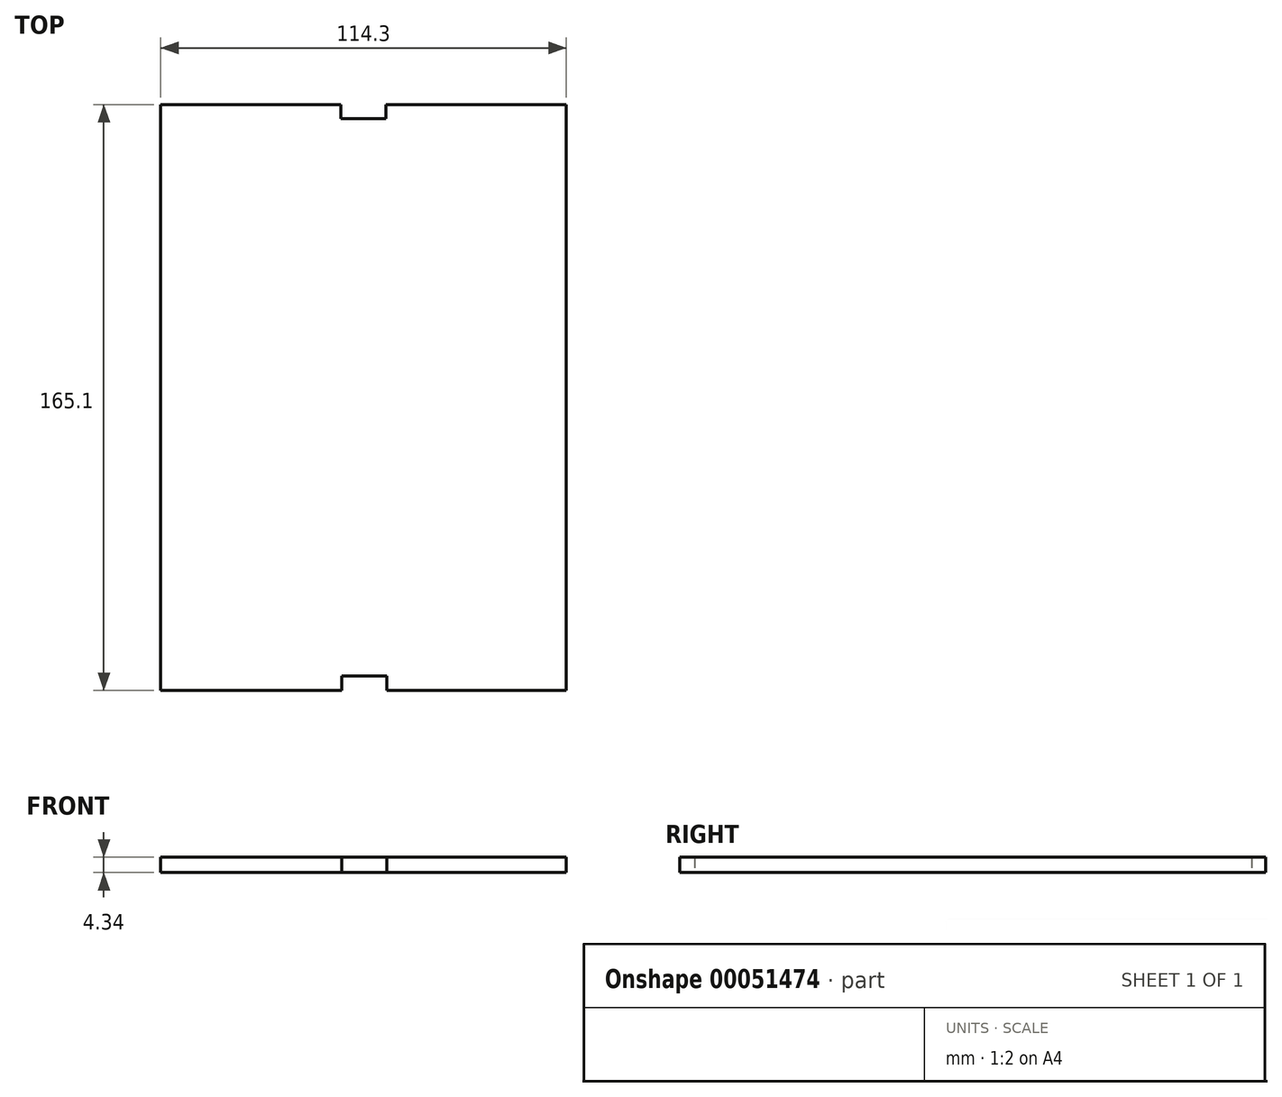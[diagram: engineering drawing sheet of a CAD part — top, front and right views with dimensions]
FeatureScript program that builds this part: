
annotation { "Feature Type Name" : "Feature", "Feature Type Description" : "" }
export const myFeature = defineFeature(function(context is Context, id is Id, definition is map)
    precondition{}
    {
        {
            var Q0;
            Q0=qCreatedBy(makeId("Top.planeOp"),FACE);
            var sketch = newSketch(context, id + "F0", { "sketchPlane" : qUnion([Q0])});
            skLineSegment(sketch, "E0.bottom", {"start": v(-56.26, 135.4) * mm, "end": v(58.04, 135.4) * mm});
            skLineSegment(sketch, "E0.top", {"start": v(-56.26, -29.7) * mm, "end": v(58.04, -29.7) * mm});
            skLineSegment(sketch, "E0.left", {"start": v(-56.26, 135.4) * mm, "end": v(-56.26, -29.7) * mm});
            skLineSegment(sketch, "E0.right", {"start": v(58.04, 135.4) * mm, "end": v(58.04, -29.7) * mm});
            skSolve(sketch);
        }
        {
            var Q0;
            Q0 = qSketchRegion(id + "F0", true);
            extrude(context, id + "F1", {"entities" : qUnion([Q0]), "depth" : 4.34 * mm});
        }
        {
            var Q0;
            Q0=qCreatedBy(makeId("Top.planeOp"),FACE);
            var sketch = newSketch(context, id + "F2", { "sketchPlane" : qUnion([Q0])});
            skLineSegment(sketch, "E1.0", {"start": v(-5.46, 135.4) * mm, "end": v(-5.46, -29.37) * mm, "construction": true});
            skLineSegment(sketch, "E2", {"start": v(-57.24, 53.01) * mm, "end": v(58.42, 53.01) * mm, "construction": true});
            skPoint(sketch, "E2.startSnap0", {"position": v(-5.46, 53.01) * mm});
            skPoint(sketch, "E3.orphan", {"position": v(7.24, 131.05) * mm});
            skPoint(sketch, "E4.MirrorCS.start.orphan", {"position": v(-5.46, 131.05) * mm});
            skPoint(sketch, "E5.orphan", {"position": v(-5.46, 135.4) * mm});
            skPoint(sketch, "E6.MirrorCS.end.orphan", {"position": v(7.24, 135.4) * mm});
            skPoint(sketch, "E7.end.orphan", {"position": v(7.24, -25.02) * mm});
            skPoint(sketch, "E8.left.end.orphan", {"position": v(-5.46, -25.02) * mm});
            skLineSegment(sketch, "E9.left", {"start": v(-5.46, 131.05) * mm, "end": v(-5.46, 135.4) * mm});
            skLineSegment(sketch, "E9.right", {"start": v(7.24, 131.05) * mm, "end": v(7.24, 135.4) * mm});
            skPoint(sketch, "E10.orphan", {"position": v(7.24, -29.37) * mm});
            skPoint(sketch, "E11.start.orphan", {"position": v(0.89, 135.4) * mm});
            skPoint(sketch, "E12.trimOffspring.end.orphan", {"position": v(0.89, -29.37) * mm});
            skSolve(sketch);
        }
        {
            var Q0;
            Q0=qCreatedBy(makeId("Top.planeOp"),FACE);
            var sketch = newSketch(context, id + "F3", { "sketchPlane" : qUnion([Q0])});
            skLineSegment(sketch, "E13.top", {"start": v(-5.18, 131.6) * mm, "end": v(7.52, 131.6) * mm});
            skLineSegment(sketch, "E13.left", {"start": v(-5.18, 135.95) * mm, "end": v(-5.18, 131.6) * mm});
            skLineSegment(sketch, "E13.right", {"start": v(7.52, 135.95) * mm, "end": v(7.52, 131.6) * mm});
            skLineSegment(sketch, "E14.MirrorCS", {"start": v(-5.18, -29.92) * mm, "end": v(7.52, -29.92) * mm});
            skLineSegment(sketch, "E15.MirrorCS", {"start": v(-5.18, -29.92) * mm, "end": v(-5.18, -25.58) * mm});
            skLineSegment(sketch, "E16.MirrorCS", {"start": v(7.52, -29.92) * mm, "end": v(7.52, -25.58) * mm});
            skLineSegment(sketch, "E17.MirrorCS", {"start": v(-5.18, -25.58) * mm, "end": v(7.52, -25.58) * mm});
            skSolve(sketch);
        }
        {
            var Q0;
            Q0 = qSketchRegion(id + "F3", true);
            extrude(context, id + "F4", {"entities" : qUnion([Q0]), "operationType" : NewBodyOperationType.REMOVE, "endBound" : BoundingType.THROUGH_ALL, "depth" : 4.34 * mm});
        }
        {
            var Q0;
            Q0=qCreatedBy(makeId("Top.planeOp"),FACE);
            var sketch = newSketch(context, id + "F5", { "sketchPlane" : qUnion([Q0])});
            skLineSegment(sketch, "E18.bottom", {"start": v(-5.45, 135.77) * mm, "end": v(7.25, 135.77) * mm});
            skLineSegment(sketch, "E18.top", {"start": v(-5.45, 131.43) * mm, "end": v(7.25, 131.43) * mm});
            skLineSegment(sketch, "E18.left", {"start": v(-5.45, 135.77) * mm, "end": v(-5.45, 131.43) * mm});
            skLineSegment(sketch, "E18.right", {"start": v(7.25, 135.77) * mm, "end": v(7.25, 131.43) * mm});
            skLineSegment(sketch, "E19", {"start": v(0, -29.45) * mm, "end": v(0, 143.66) * mm, "construction": true});
            skSolve(sketch);
        }
        {
            var Q0;
            Q0 = qSketchRegion(id + "F5", true);
            extrude(context, id + "F6", {"entities" : qUnion([Q0]), "operationType" : NewBodyOperationType.REMOVE, "endBound" : BoundingType.THROUGH_ALL, "depth" : 25.4 * mm});
        }
    });
